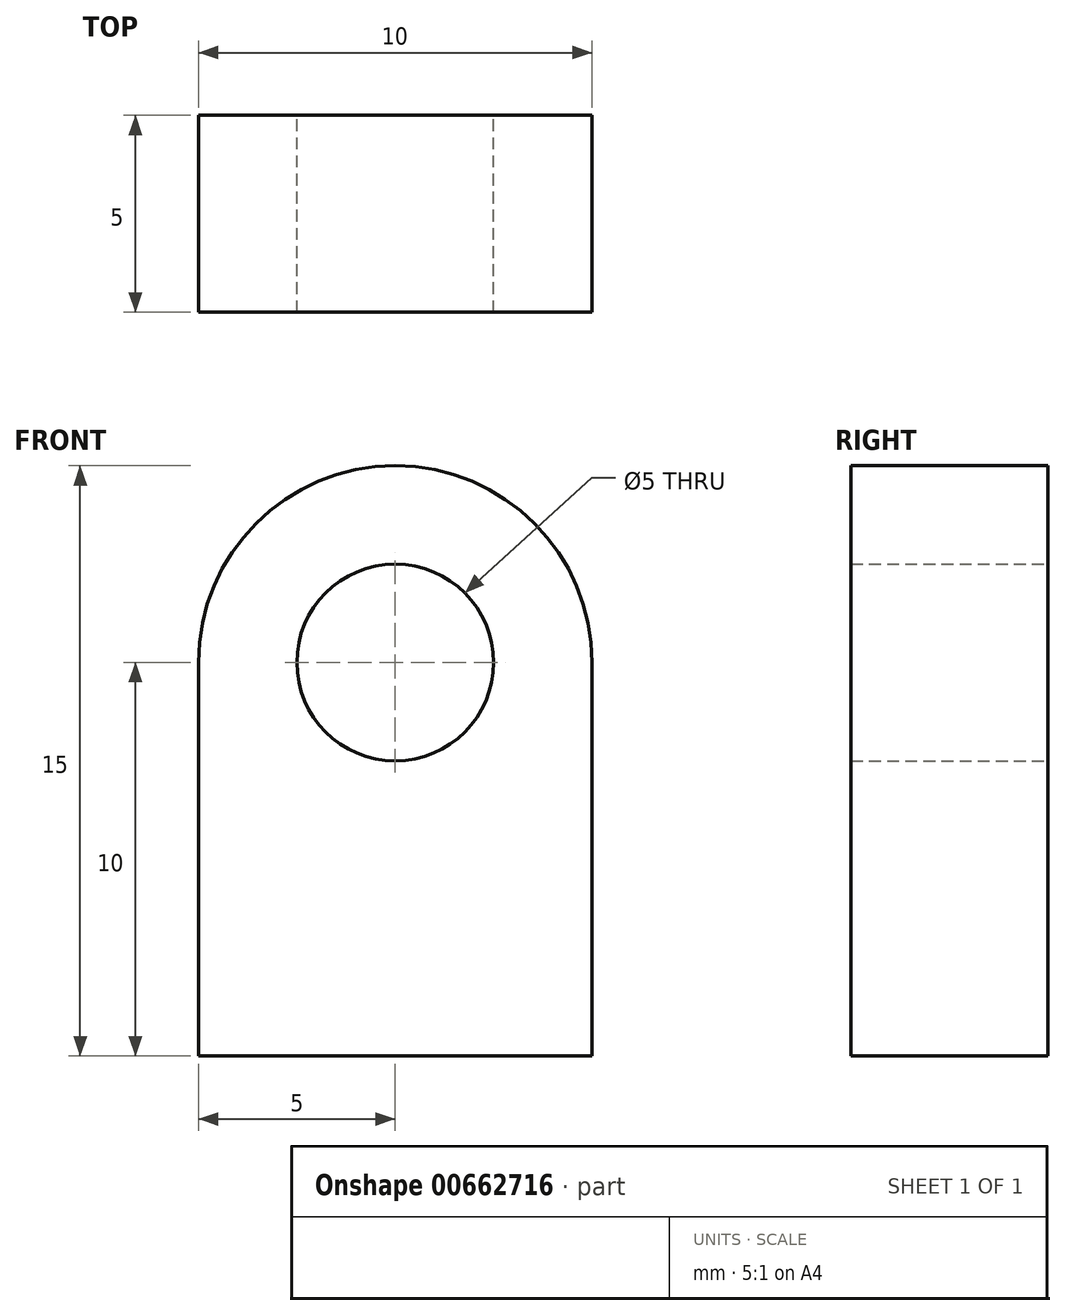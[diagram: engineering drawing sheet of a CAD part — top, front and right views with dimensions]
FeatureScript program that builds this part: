
annotation { "Feature Type Name" : "Feature", "Feature Type Description" : "" }
export const myFeature = defineFeature(function(context is Context, id is Id, definition is map)
    precondition{}
    {
        {
            var Q0;
            Q0=qCreatedBy(makeId("Front.planeOp"),FACE);
            var sketch = newSketch(context, id + "F0", { "sketchPlane" : qUnion([Q0])});
            skCircle(sketch, "E0", {"center": v(0, 0) * mm, "radius": 2.5 * mm});
            skArc(sketch, "E1", {"start": v(5, 0) * mm, "mid": v(0, 5) * mm, "end": v(-5, 0) * mm});
            skLineSegment(sketch, "E2.bottom", {"start": v(-5, 0) * mm, "end": v(5, 0) * mm});
            skLineSegment(sketch, "E2.top", {"start": v(-5, -10) * mm, "end": v(5, -10) * mm});
            skLineSegment(sketch, "E2.left", {"start": v(-5, 0) * mm, "end": v(-5, -10) * mm});
            skLineSegment(sketch, "E2.right", {"start": v(5, 0) * mm, "end": v(5, -10) * mm});
            skSolve(sketch);
        }
        {
            var Q0;
            Q0=makeQuery(id+"F0.imprint","IMPRINT",FACE,{"disambiguationData":[TD([[makeQuery(id+"F0.imprint","IMPRINT",EDGE,{"derivedFrom":sQuery(id+"F0.wireOp",EDGE,"E2.top")}),1.0]])]});
            var Q1;
            {var subQ4=sQuery(id+"F0.wireOp",EDGE,"E1");Q1=makeQuery(id+"F0.imprint","IMPRINT",FACE,{"disambiguationData":[TD([[makeQuery(id+"F0.imprint","IMPRINT",EDGE,{"derivedFrom":subQ4}),1.0]])]});}
            extrude(context, id + "F1", {"entities" : qUnion([Q0, Q1]), "depth" : 5 * mm, "offsetDistance" : 25 * mm});
        }
    });
